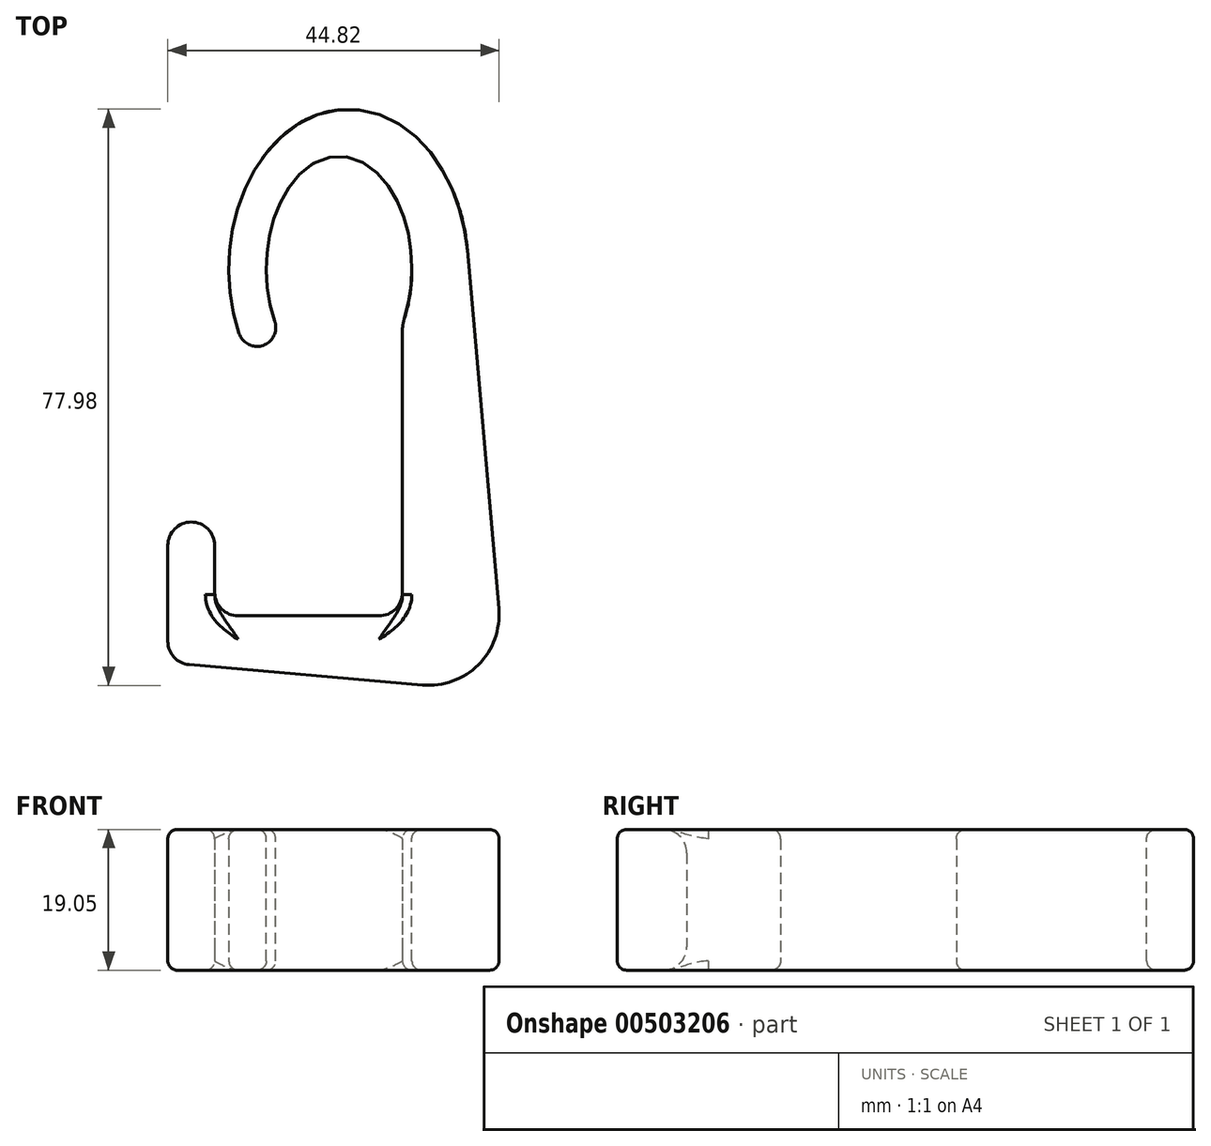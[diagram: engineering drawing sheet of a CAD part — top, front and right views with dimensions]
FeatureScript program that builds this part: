
annotation { "Feature Type Name" : "Feature", "Feature Type Description" : "" }
export const myFeature = defineFeature(function(context is Context, id is Id, definition is map)
    precondition{}
    {
        {
            var Q0;
            Q0=qCreatedBy(makeId("Top.planeOp"),FACE);
            var sketch = newSketch(context, id + "F0", { "sketchPlane" : qUnion([Q0])});
            skEllipse(sketch, "E0", {"center": v(0, 0) * mm, "majorRadius": 15.24 * mm, "minorRadius": 9.84 * mm, "majorAxis": v(0, 1)});
            skPoint(sketch, "E1", {"position": v(0, 21.59) * mm});
            skPoint(sketch, "E2", {"position": v(16.2, 0) * mm});
            skPoint(sketch, "E3", {"position": v(0, 15.24) * mm});
            skPoint(sketch, "E4", {"position": v(9.84, 0) * mm});
            skLineSegment(sketch, "E5", {"start": v(-8.57, -7.49) * mm, "end": v(-8.57, -17.14) * mm});
            skPoint(sketch, "E6", {"position": v(-9.84, 0) * mm});
            skLineSegment(sketch, "E7", {"start": v(8.57, -47) * mm, "end": v(-16.83, -47) * mm});
            skLineSegment(sketch, "E8", {"start": v(-20.28, -53.6) * mm, "end": v(11.28, -56.35) * mm});
            skLineSegment(sketch, "E9", {"start": v(8.57, -47) * mm, "end": v(8.57, -7.49) * mm});
            skPoint(sketch, "E10", {"position": v(0, -15.24) * mm});
            skLineSegment(sketch, "E11", {"start": v(-16.83, -47) * mm, "end": v(-16.83, -37.46) * mm});
            skArc(sketch, "E12", {"start": v(-16.83, -37.46) * mm, "mid": v(-20, -34.3) * mm, "end": v(-23.18, -37.46) * mm});
            skLineSegment(sketch, "E13", {"start": v(-23.18, -50.43) * mm, "end": v(-23.18, -37.46) * mm});
            skLineSegment(sketch, "E14", {"start": v(21.6, -46.04) * mm, "end": v(17.35, 2.5) * mm});
            skPoint(sketch, "E15.visualSharp", {"position": v(-23.18, -53.34) * mm});
            skArc(sketch, "E15.filletArc", {"start": v(-23.18, -50.43) * mm, "mid": v(-22.34, -52.58) * mm, "end": v(-20.28, -53.6) * mm});
            skPoint(sketch, "E16.visualSharp", {"position": v(22.59, -57.34) * mm});
            skArc(sketch, "E16.filletArc", {"start": v(11.28, -56.35) * mm, "mid": v(18.85, -53.6) * mm, "end": v(21.6, -46.04) * mm});
            skEllipse(sketch, "E17", {"center": v(1.27, 0) * mm, "majorRadius": 21.59 * mm, "minorRadius": 16.2 * mm, "majorAxis": v(0, 1)});
            skPoint(sketch, "E18", {"position": v(-14.92, 0) * mm});
            skPoint(sketch, "E19", {"position": v(1.27, 21.59) * mm});
            skPoint(sketch, "E20", {"position": v(17.46, 0) * mm});
            skPoint(sketch, "E21", {"position": v(1.27, -21.59) * mm});
            skSolve(sketch);
        }
        {
            var Q0;
            {var subQ0=sQuery(id+"F0.wireOp",EDGE,"E5");Q0=makeQuery(id+"F0.imprint","IMPRINT",FACE,{"disambiguationData":[TD([[makeQuery(id+"F0.imprint","IMPRINT",EDGE,{"derivedFrom":subQ0}),-1.0]])]});}
            var Q1;
            Q1=makeQuery(id+"F0.imprint","IMPRINT",FACE,{"disambiguationData":[TD([[makeQuery(id+"F0.imprint","IMPRINT",EDGE,{"derivedFrom":sQuery(id+"F0.wireOp",EDGE,"E7")}),1.0]])]});
            extrude(context, id + "F1", {"entities" : qUnion([Q0, Q1]), "depth" : 19.05 * mm});
        }
        {
            var Q0;
            Q0=makeQuery(id+"F1.opExtrude","SWEPT_EDGE",EDGE,{"disambiguationData":[OSD([sQuery(id+"F0.wireOp",EDGE,"p04lJhMv-mDid-4yFg-3mYq-FFe39wJucyhK"),sQuery(id+"F0.wireOp",EDGE,"E5")])]});
            fillet(context, id + "F2", {"entities" : qUnion([Q0]), "radius" : 2.54 * mm, "tangentPropagation" : true, "allowEdgeOverflow" : false});
        }
        {
            var Q0;
            Q0=makeQuery(id+"F1.opExtrude","SWEPT_EDGE",EDGE,{"disambiguationData":[OSD([sQuery(id+"F0.wireOp",EDGE,"E0"),sQuery(id+"F0.wireOp",EDGE,"E5")])]});
            var Q1;
            Q1=makeQuery(id+"F1.opExtrude","SWEPT_EDGE",EDGE,{"disambiguationData":[OSD([sQuery(id+"F0.wireOp",EDGE,"E0"),sQuery(id+"F0.wireOp",EDGE,"opYENdNi-ipUp-i5Ez-ItB4-cHX9BlymKPIz")])]});
            fillet(context, id + "F3", {"entities" : qUnion([Q0, Q1]), "radius" : 5.08 * mm, "tangentPropagation" : true, "allowEdgeOverflow" : false});
        }
        {
            var Q0;
            Q0=makeQuery(id+"F1.opExtrude","CAP_EDGE",EDGE,{"disambiguationData":[OSD([sQuery(id+"F0.wireOp",EDGE,"E7")])],"isStart":false});
            var Q1;
            Q1=makeQuery(id+"F1.opExtrude","CAP_EDGE",EDGE,{"disambiguationData":[OSD([sQuery(id+"F0.wireOp",EDGE,"E7")])],"isStart":true});
            fillet(context, id + "F4", {"entities" : qUnion([Q0, Q1]), "radius" : 3.17 * mm, "tangentPropagation" : true, "allowEdgeOverflow" : false});
        }
        {
            var Q0;
            Q0=makeQuery(id+"F1.opExtrude","SWEPT_EDGE",EDGE,{"disambiguationData":[OSD([sQuery(id+"F0.wireOp",EDGE,"E7"),sQuery(id+"F0.wireOp",EDGE,"E9")])]});
            var Q1;
            Q1=makeQuery(id+"F1.opExtrude","SWEPT_EDGE",EDGE,{"disambiguationData":[OSD([sQuery(id+"F0.wireOp",EDGE,"E7"),sQuery(id+"F0.wireOp",EDGE,"E11")])]});
            fillet(context, id + "F5", {"entities" : qUnion([Q0, Q1]), "radius" : 3.17 * mm, "tangentPropagation" : true, "allowEdgeOverflow" : false});
        }
        {
            var Q0;
            Q0=makeQuery(id+"F1.opExtrude","CAP_EDGE",EDGE,{"disambiguationData":[OSD([sQuery(id+"F0.wireOp",EDGE,"E9")])],"isStart":false});
            var Q1;
            Q1=makeQuery(id+"F1.opExtrude","CAP_EDGE",EDGE,{"disambiguationData":[OSD([sQuery(id+"F0.wireOp",EDGE,"E13")])],"isStart":true});
            fillet(context, id + "F6", {"entities" : qUnion([Q0, Q1]), "radius" : 1.27 * mm, "tangentPropagation" : true, "allowEdgeOverflow" : false});
        }
    });
